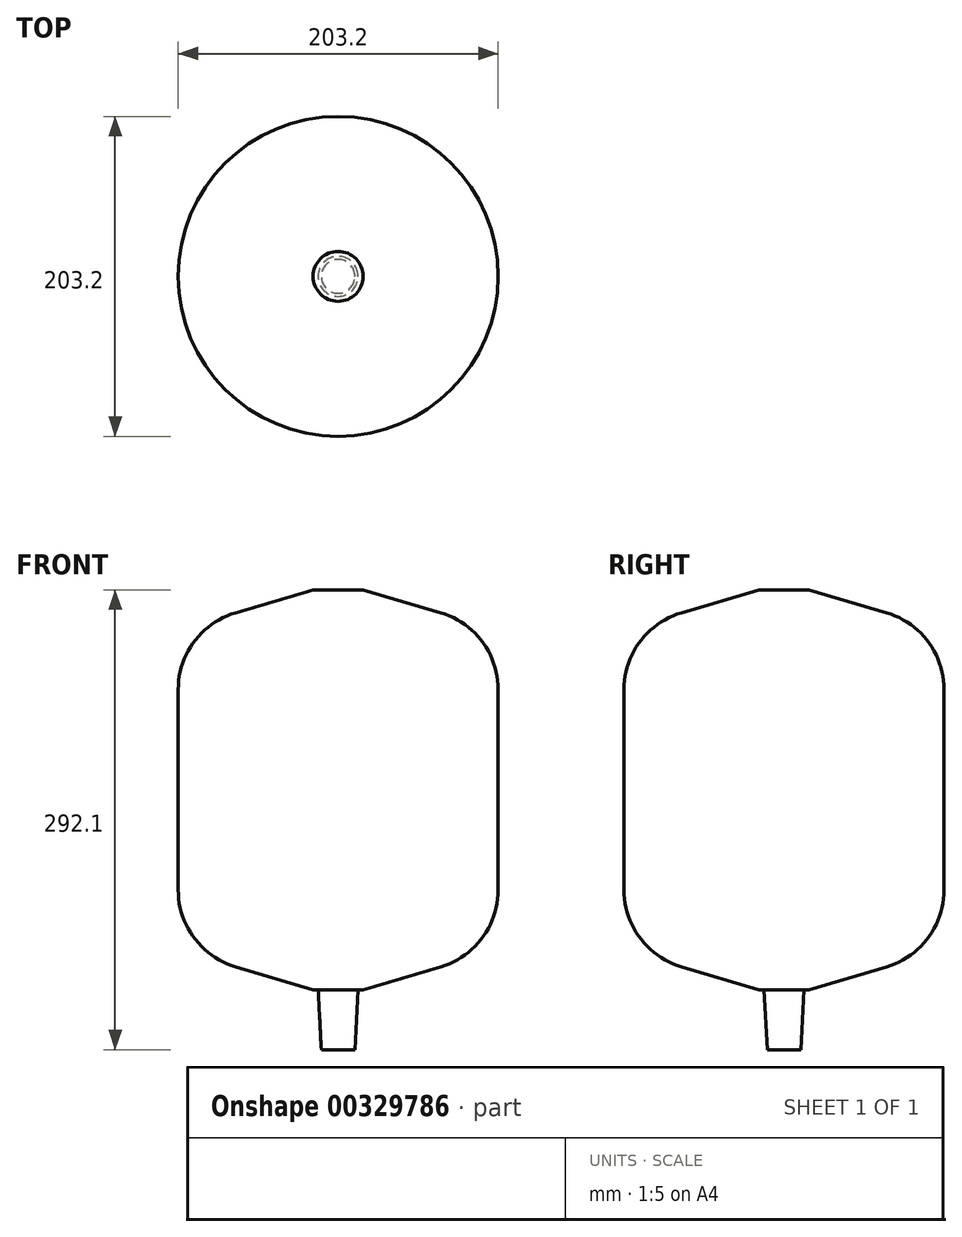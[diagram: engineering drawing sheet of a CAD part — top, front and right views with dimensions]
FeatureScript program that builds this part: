
annotation { "Feature Type Name" : "Feature", "Feature Type Description" : "" }
export const myFeature = defineFeature(function(context is Context, id is Id, definition is map)
    precondition{}
    {
        {
            var Q0;
            Q0=qCreatedBy(makeId("Top.planeOp"),FACE);
            var sketch = newSketch(context, id + "F0", { "sketchPlane" : qUnion([Q0])});
            skCircle(sketch, "E0", {"center": v(0, 0) * mm, "radius": 101.6 * mm});
            skSolve(sketch);
        }
        {
            var Q0;
            Q0 = qSketchRegion(id + "F0", true);
            extrude(context, id + "F1", {"entities" : qUnion([Q0]), "depth" : 254 * mm});
        }
        {
            var Q0;
            Q0=makeQuery(id+"F1.opExtrude","CAP_FACE",FACE,{"disambiguationData":[OSD([sQuery(id+"F0.wireOp",EDGE,"E0")])],"isStart":true});
            var sketch = newSketch(context, id + "F2", { "sketchPlane" : qUnion([Q0])});
            skCircle(sketch, "E1", {"center": v(0, 0) * mm, "radius": 12.7 * mm});
            skSolve(sketch);
        }
        {
            var Q0;
            Q0 = qSketchRegion(id + "F2", true);
            extrude(context, id + "F3", {"entities" : qUnion([Q0]), "operationType" : NewBodyOperationType.ADD, "depth" : 38.1 * mm, "hasDraft" : true, "draftAngle" : 3 * degree, "draftPullDirection" : true});
        }
        {
            var Q0;
            Q0=makeQuery(id+"F1.opExtrude","CAP_FACE",FACE,{"disambiguationData":[OSD([sQuery(id+"F0.wireOp",EDGE,"E0")])],"isStart":false});
            var Q1;
            Q1=makeQuery(id+"F1.opExtrude","CAP_EDGE",EDGE,{"disambiguationData":[OSD([sQuery(id+"F0.wireOp",EDGE,"E0")])],"isStart":true});
            chamfer(context, id + "F4", {"entities" : qUnion([Q0, Q1]), "chamferType" : ChamferType.TWO_OFFSETS, "width1" : 85.72 * mm, "oppositeDirection" : false, "width2" : 25.4 * mm, "tangentPropagation" : true});
        }
        {
            var Q0;
            {var subQ0=sQuery(id+"F0.wireOp",EDGE,"E0");Q0=makeQuery(id+"F4.opChamfer","BLEND_EDGE",EDGE,{"blendedFrom":[makeQuery(id+"F1.opExtrude","CAP_EDGE",EDGE,{"disambiguationData":[OSD([subQ0])],"isStart":true}),makeQuery(id+"F1.opExtrude","SWEPT_FACE",FACE,{"disambiguationData":[OSD([subQ0])]})],"blendedInto":[makeQuery(id+"F1.opExtrude","SWEPT_FACE",FACE,{"disambiguationData":[OSD([subQ0])]})]});}
            var Q1;
            {var subQ0=sQuery(id+"F0.wireOp",EDGE,"E0");Q1=makeQuery(id+"F4.opChamfer","BLEND_EDGE",EDGE,{"blendedFrom":[makeQuery(id+"F1.opExtrude","CAP_EDGE",EDGE,{"disambiguationData":[OSD([subQ0])],"isStart":false}),makeQuery(id+"F1.opExtrude","SWEPT_FACE",FACE,{"disambiguationData":[OSD([subQ0])]})],"blendedInto":[makeQuery(id+"F1.opExtrude","SWEPT_FACE",FACE,{"disambiguationData":[OSD([subQ0])]})]});}
            fillet(context, id + "F5", {"entities" : qUnion([Q0, Q1]), "radius" : 50.8 * mm, "tangentPropagation" : true, "allowEdgeOverflow" : false});
        }
    });
